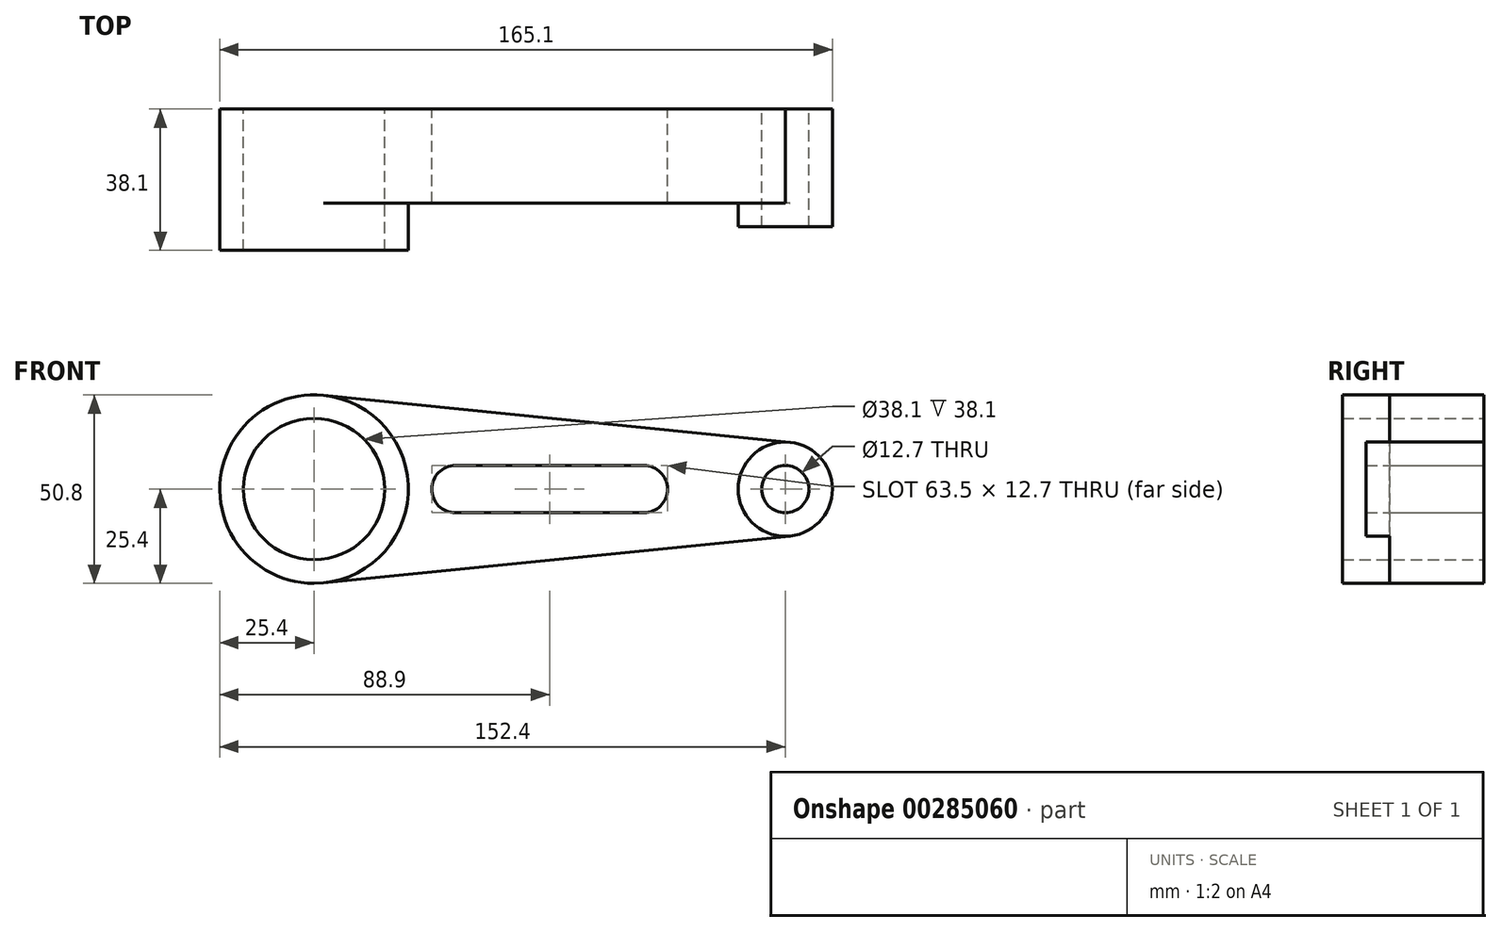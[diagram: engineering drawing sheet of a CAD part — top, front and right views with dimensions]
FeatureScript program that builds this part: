
annotation { "Feature Type Name" : "Feature", "Feature Type Description" : "" }
export const myFeature = defineFeature(function(context is Context, id is Id, definition is map)
    precondition{}
    {
        {
            var Q0;
            Q0=qCreatedBy(makeId("Front.planeOp"),FACE);
            var sketch = newSketch(context, id + "F0", { "sketchPlane" : qUnion([Q0])});
            skCircle(sketch, "E0", {"center": v(0, 0) * mm, "radius": 19.05 * mm});
            skCircle(sketch, "E1", {"center": v(0, 0) * mm, "radius": 25.4 * mm});
            skLineSegment(sketch, "E2", {"start": v(0, 0) * mm, "end": v(25.4, 0) * mm});
            skCircle(sketch, "E3", {"center": v(127, 0) * mm, "radius": 6.35 * mm});
            skCircle(sketch, "E4", {"center": v(127, 0) * mm, "radius": 12.7 * mm});
            skPoint(sketch, "E5", {"position": v(127, 12.7) * mm});
            skPoint(sketch, "E6", {"position": v(128.27, -12.64) * mm});
            skLineSegment(sketch, "E7", {"start": v(127, 12.7) * mm, "end": v(0, 25.53) * mm});
            skLineSegment(sketch, "E8", {"start": v(128.27, -12.64) * mm, "end": v(0, -25.53) * mm});
            skArc(sketch, "E9", {"start": v(38.1, 6.35) * mm, "mid": v(31.75, 0) * mm, "end": v(38.1, -6.35) * mm});
            skArc(sketch, "E10", {"start": v(88.9, -6.35) * mm, "mid": v(95.25, 0) * mm, "end": v(88.9, 6.35) * mm});
            skLineSegment(sketch, "E11", {"start": v(88.9, 6.35) * mm, "end": v(38.1, 6.35) * mm});
            skLineSegment(sketch, "E12", {"start": v(88.9, -6.35) * mm, "end": v(38.1, -6.35) * mm});
            skPoint(sketch, "E13", {"position": v(31.75, 0) * mm});
            skSolve(sketch);
        }
        {
            var Q0;
            Q0=makeQuery(id+"F0.imprint","IMPRINT",FACE,{"disambiguationData":[TD([[makeQuery(id+"F0.imprint","IMPRINT",EDGE,{"derivedFrom":sQuery(id+"F0.wireOp",EDGE,"E0")}),-1.0]])]});
            extrude(context, id + "F1", {"entities" : qUnion([Q0]), "depth" : 38.1 * mm});
        }
        {
            var Q0;
            Q0=makeQuery(id+"F0.imprint","IMPRINT",FACE,{"disambiguationData":[TD([[makeQuery(id+"F0.imprint","IMPRINT",EDGE,{"derivedFrom":sQuery(id+"F0.wireOp",EDGE,"E9")}),-1.0]])]});
            extrude(context, id + "F2", {"entities" : qUnion([Q0]), "operationType" : NewBodyOperationType.ADD, "depth" : 25.4 * mm});
        }
        {
            var Q0;
            Q0=makeQuery(id+"F0.imprint","IMPRINT",FACE,{"disambiguationData":[TD([[makeQuery(id+"F0.imprint","IMPRINT",EDGE,{"derivedFrom":sQuery(id+"F0.wireOp",EDGE,"E3")}),-1.0]])]});
            extrude(context, id + "F3", {"entities" : qUnion([Q0]), "operationType" : NewBodyOperationType.ADD, "depth" : 31.75 * mm});
        }
    });
